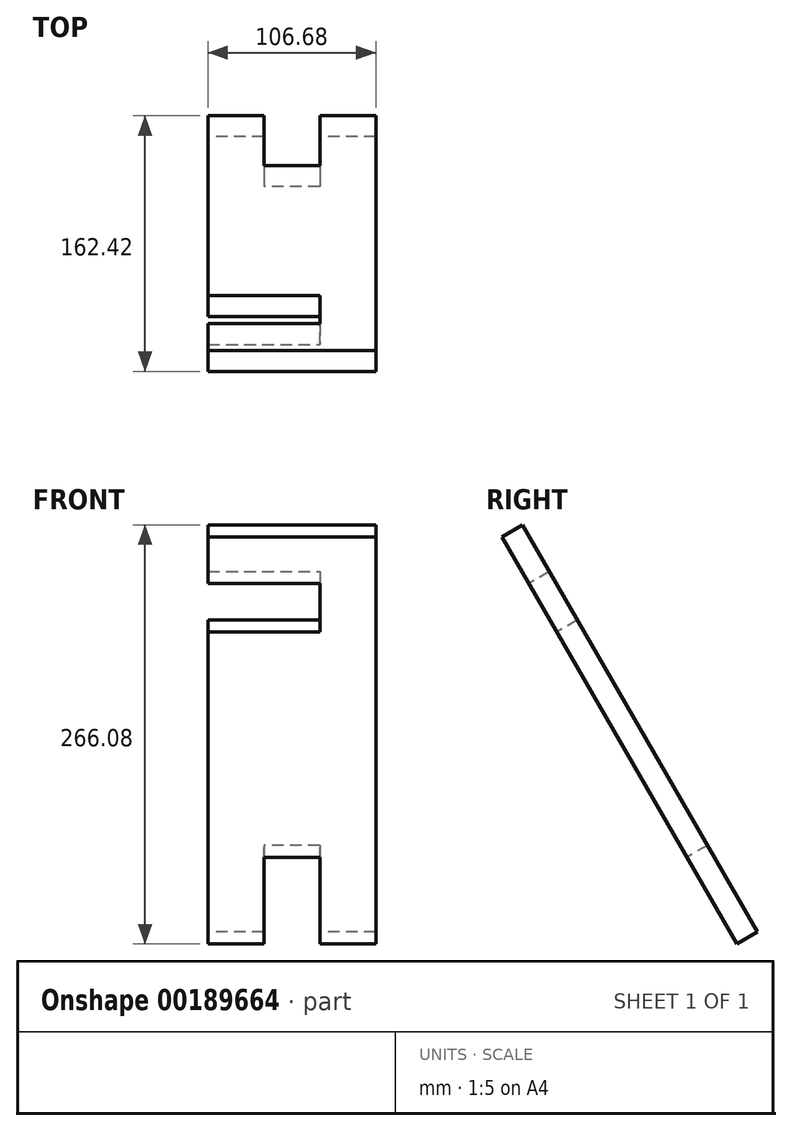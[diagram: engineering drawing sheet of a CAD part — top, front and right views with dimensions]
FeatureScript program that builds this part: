
annotation { "Feature Type Name" : "Feature", "Feature Type Description" : "" }
export const myFeature = defineFeature(function(context is Context, id is Id, definition is map)
    precondition{}
    {
        {
            var Q0;
            Q0=qCreatedBy(makeId("Top.planeOp"),FACE);
            var sketch = newSketch(context, id + "F0", { "sketchPlane" : qUnion([Q0])});
            skLineSegment(sketch, "E0", {"start": v(-45.42, 0) * mm, "end": v(56.18, 0) * mm});
            skSolve(sketch);
        }
        {
            var Q0;
            Q0=sQuery(id+"F0.wireOp",EDGE,"E0");
            cPlane(context, id + "F1", {"entities" : qUnion([Q0]), "cplaneType" : CPlaneType.LINE_ANGLE, "offset" : 25.4 * mm, "angle" : 30 * degree, "width" : 152.4 * mm, "height" : 152.4 * mm});
        }
        {
            var Q0;
            Q0=qCreatedBy(id+"F1.planeOp",FACE);
            var sketch = newSketch(context, id + "F2", { "sketchPlane" : qUnion([Q0])});
            skLineSegment(sketch, "E1.bottom", {"start": v(-53.34, 149.23) * mm, "end": v(53.34, 149.23) * mm});
            skLineSegment(sketch, "E1.top", {"start": v(-53.34, -149.23) * mm, "end": v(53.34, -149.23) * mm});
            skLineSegment(sketch, "E1.left", {"start": v(-53.34, 149.23) * mm, "end": v(-53.34, -149.23) * mm});
            skLineSegment(sketch, "E1.right", {"start": v(53.34, 149.22) * mm, "end": v(53.34, -149.23) * mm});
            skPoint(sketch, "E1.middle", {"position": v(0, 0) * mm});
            skLineSegment(sketch, "E2.bottom", {"start": v(53.34, 114.94) * mm, "end": v(-17.78, 114.94) * mm});
            skLineSegment(sketch, "E2.top", {"start": v(53.34, 79.38) * mm, "end": v(-17.78, 79.38) * mm});
            skLineSegment(sketch, "E2.left", {"start": v(53.34, 114.94) * mm, "end": v(53.34, 79.38) * mm});
            skLineSegment(sketch, "E2.right", {"start": v(-17.78, 114.94) * mm, "end": v(-17.78, 79.38) * mm});
            skLineSegment(sketch, "E3.bottom", {"start": v(-17.78, -149.23) * mm, "end": v(17.78, -149.23) * mm});
            skLineSegment(sketch, "E3.top", {"start": v(-17.78, -85.73) * mm, "end": v(17.78, -85.73) * mm});
            skLineSegment(sketch, "E3.left", {"start": v(-17.78, -149.23) * mm, "end": v(-17.78, -85.73) * mm});
            skLineSegment(sketch, "E3.right", {"start": v(17.78, -149.23) * mm, "end": v(17.78, -85.73) * mm});
            skLineSegment(sketch, "E4", {"start": v(-17.78, -85.73) * mm, "end": v(-53.34, -85.73) * mm});
            skSolve(sketch);
        }
        {
            var Q0;
            {var subQ1=sQuery(id+"F2.wireOp",EDGE,"E1.bottom");Q0=makeQuery(id+"F2.imprint","IMPRINT",FACE,{"disambiguationData":[TD([[makeQuery(id+"F2.imprint","IMPRINT",EDGE,{"derivedFrom":subQ1}),-1.0]])]});}
            var Q1;
            {var subQ3=sQuery(id+"F2.wireOp",EDGE,"E3.left");Q1=makeQuery(id+"F2.imprint","IMPRINT",FACE,{"disambiguationData":[TD([[makeQuery(id+"F2.imprint","IMPRINT",EDGE,{"derivedFrom":subQ3}),1.0]])]});}
            extrude(context, id + "F3", {"entities" : qUnion([Q0, Q1]), "depth" : 15.24 * mm});
        }
    });
